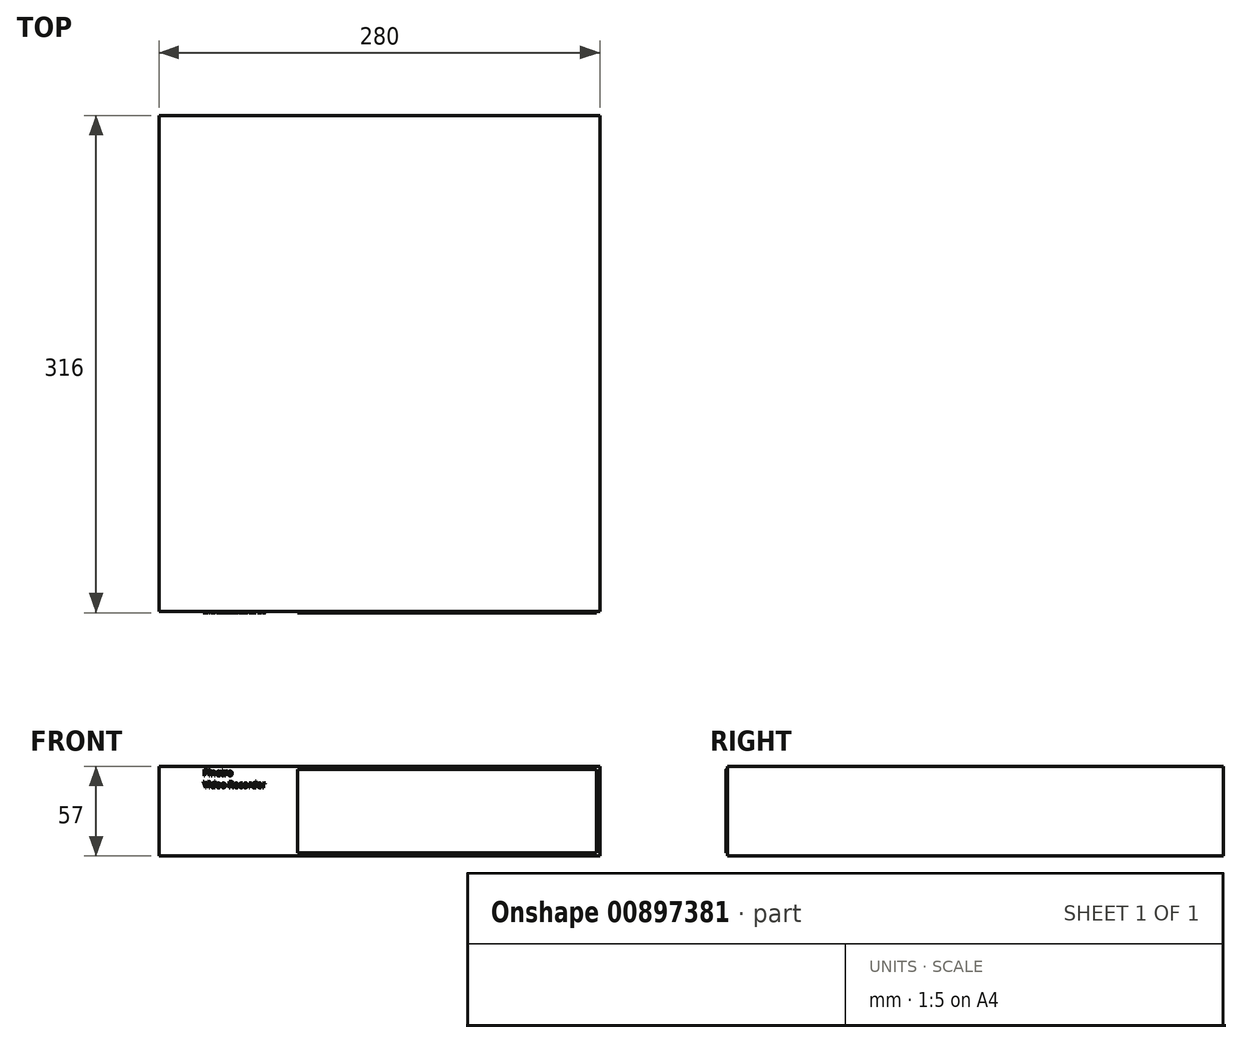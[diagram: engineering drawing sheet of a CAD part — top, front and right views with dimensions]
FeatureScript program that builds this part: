
annotation { "Feature Type Name" : "Feature", "Feature Type Description" : "" }
export const myFeature = defineFeature(function(context is Context, id is Id, definition is map)
    precondition{}
    {
        {
            var Q0;
            Q0=qCreatedBy(makeId("Top.planeOp"),FACE);
            var sketch = newSketch(context, id + "F0", { "sketchPlane" : qUnion([Q0])});
            skLineSegment(sketch, "E0.bottom", {"start": v(0, 0) * mm, "end": v(-280, 0) * mm});
            skLineSegment(sketch, "E0.top", {"start": v(0, 315) * mm, "end": v(-280, 315) * mm});
            skLineSegment(sketch, "E0.left", {"start": v(0, 0) * mm, "end": v(0, 315) * mm});
            skLineSegment(sketch, "E0.right", {"start": v(-280, 0) * mm, "end": v(-280, 315) * mm});
            skSolve(sketch);
        }
        {
            var Q0;
            Q0 = qSketchRegion(id + "F0", true);
            extrude(context, id + "F1", {"entities" : qUnion([Q0]), "depth" : 57 * mm, "offsetDistance" : 25 * mm});
        }
        {
            var Q0;
            Q0=makeQuery(id+"F1.opExtrude","SWEPT_FACE",FACE,{"disambiguationData":[OSD([sQuery(id+"F0.wireOp",EDGE,"E0.bottom")])]});
            var sketch = newSketch(context, id + "F2", { "sketchPlane" : qUnion([Q0])});
            skLineSegment(sketch, "E1.bottom", {"start": v(-192, 55) * mm, "end": v(-2, 55) * mm});
            skLineSegment(sketch, "E1.top", {"start": v(-192, 2) * mm, "end": v(-2, 2) * mm});
            skLineSegment(sketch, "E1.left", {"start": v(-192, 55) * mm, "end": v(-192, 2) * mm});
            skLineSegment(sketch, "E1.right", {"start": v(-2, 55) * mm, "end": v(-2, 2) * mm});
            skText(sketch, "E2", { "text": "Pinetro \nVideo Recorder", "fontName": "OpenSans-Regular.ttf"});
            const initialGuessF2  = {"E2": [-0.252, 0.051, 1, 0, 0.004]};
            skSetInitialGuess(sketch, initialGuessF2);
            skSolve(sketch);
        }
        {
            var Q0;
            Q0 = qSketchRegion(id + "F2", true);
            extrude(context, id + "F3", {"entities" : qUnion([Q0]), "operationType" : NewBodyOperationType.ADD, "depth" : 1 * mm, "offsetDistance" : 25 * mm});
        }
    });
